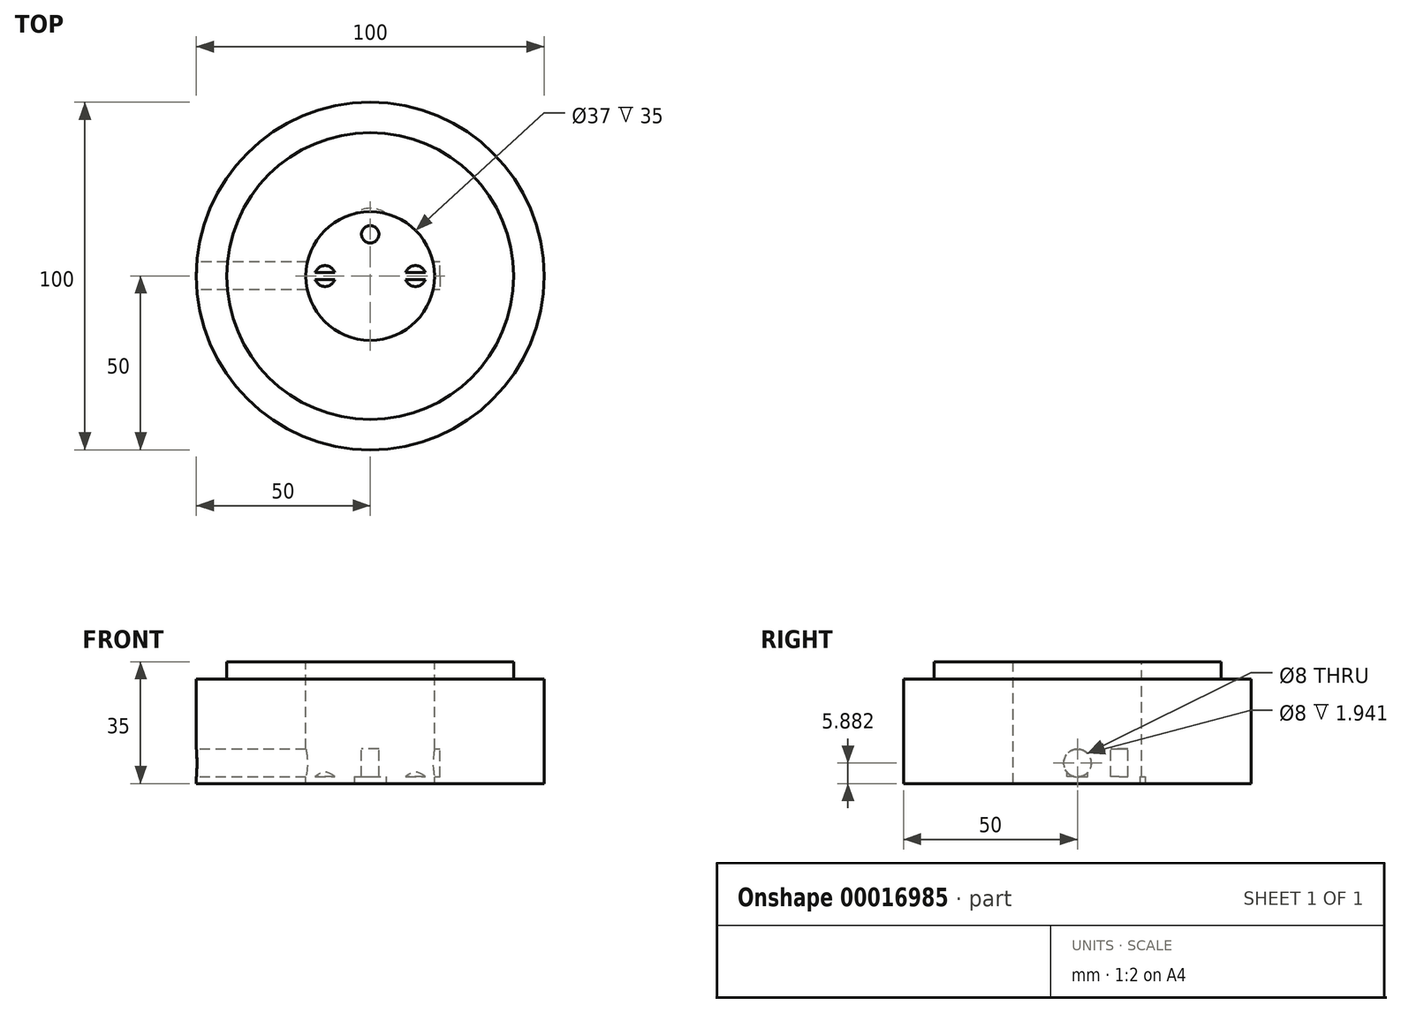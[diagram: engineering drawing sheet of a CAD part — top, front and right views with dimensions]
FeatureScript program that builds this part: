
annotation { "Feature Type Name" : "Feature", "Feature Type Description" : "" }
export const myFeature = defineFeature(function(context is Context, id is Id, definition is map)
    precondition{}
    {
        {
            var Q0;
            Q0=qCreatedBy(makeId("Top.planeOp"),FACE);
            var sketch = newSketch(context, id + "F0", { "sketchPlane" : qUnion([Q0])});
            skCircle(sketch, "E0", {"center": v(0, 0) * mm, "radius": 50 * mm});
            skSolve(sketch);
        }
        {
            var Q0;
            Q0=makeQuery(id+"F0.imprint","IMPRINT",FACE,{"disambiguationData":[TD([[makeQuery(id+"F0.imprint","IMPRINT",EDGE,{"derivedFrom":sQuery(id+"F0.wireOp",EDGE,"E0")}),1.0]])]});
            extrude(context, id + "F1", {"entities" : qUnion([Q0]), "depth" : 35 * mm});
        }
        {
            var Q0;
            Q0=makeQuery(id+"F1.opExtrude","CAP_FACE",FACE,{"disambiguationData":[OSD([sQuery(id+"F0.wireOp",EDGE,"E0")])],"isStart":false});
            var sketch = newSketch(context, id + "F2", { "sketchPlane" : qUnion([Q0])});
            skCircle(sketch, "E1", {"center": v(0, 0) * mm, "radius": 18.5 * mm});
            skSolve(sketch);
        }
        {
            var Q0;
            Q0=makeQuery(id+"F2.imprint","IMPRINT",FACE,{"disambiguationData":[TD([[makeQuery(id+"F2.imprint","IMPRINT",EDGE,{"derivedFrom":sQuery(id+"F2.wireOp",EDGE,"E1")}),1.0]])]});
            extrude(context, id + "F3", {"entities" : qUnion([Q0]), "operationType" : NewBodyOperationType.REMOVE, "oppositeDirection" : true, "depth" : 25 * mm});
        }
        {
            var Q0;
            Q0=makeQuery(id+"F1.opExtrude","CAP_FACE",FACE,{"disambiguationData":[OSD([sQuery(id+"F0.wireOp",EDGE,"E0")])],"isStart":false});
            var sketch = newSketch(context, id + "F4", { "sketchPlane" : qUnion([Q0])});
            skCircle(sketch, "E2", {"center": v(0, 0) * mm, "radius": 41.25 * mm});
            skCircle(sketch, "E3", {"center": v(0, 0) * mm, "radius": 50 * mm});
            skSolve(sketch);
        }
        {
            var Q0;
            Q0=makeQuery(id+"F4.imprint","IMPRINT",FACE,{"disambiguationData":[TD([[makeQuery(id+"F4.imprint","IMPRINT",EDGE,{"derivedFrom":sQuery(id+"F4.wireOp",EDGE,"E2")}),-1.0]])]});
            extrude(context, id + "F5", {"entities" : qUnion([Q0]), "operationType" : NewBodyOperationType.REMOVE, "oppositeDirection" : true, "depth" : 5 * mm});
        }
        {
            var Q0;
            Q0=qCreatedBy(makeId("Right.planeOp"),FACE);
            cPlane(context, id + "F6", {"entities" : qUnion([Q0]), "cplaneType" : CPlaneType.OFFSET, "offset" : 50 * mm, "oppositeDirection" : true, "width" : 150 * mm, "height" : 150 * mm});
        }
        {
            var Q0;
            Q0=qCreatedBy(id+"F6.planeOp",FACE);
            var sketch = newSketch(context, id + "F7", { "sketchPlane" : qUnion([Q0])});
            skCircle(sketch, "E4", {"center": v(0, 5.88) * mm, "radius": 4 * mm});
            skSolve(sketch);
        }
        {
            var Q0;
            Q0=makeQuery(id+"F7.imprint","IMPRINT",FACE,{"disambiguationData":[TD([[makeQuery(id+"F7.imprint","IMPRINT",EDGE,{"derivedFrom":sQuery(id+"F7.wireOp",EDGE,"E4")}),1.0]])]});
            extrude(context, id + "F8", {"entities" : qUnion([Q0]), "operationType" : NewBodyOperationType.REMOVE, "depth" : 70 * mm});
        }
        {
            var Q0;
            Q0=makeQuery(id+"F3.boolean.opBoolean","COPY",FACE,{"derivedFrom":makeQuery(id+"F3.opExtrude","CAP_FACE",FACE,{"disambiguationData":[OSD([sQuery(id+"F2.wireOp",EDGE,"E1")])],"isStart":false})});
            var sketch = newSketch(context, id + "F9", { "sketchPlane" : qUnion([Q0])});
            skCircle(sketch, "E5", {"center": v(-13, 0) * mm, "radius": 3 * mm});
            skCircle(sketch, "E6", {"center": v(13, 0) * mm, "radius": 3 * mm});
            skSolve(sketch);
        }
        {
            var Q0;
            Q0=makeQuery(id+"F9.imprint","IMPRINT",FACE,{"disambiguationData":[TD([[makeQuery(id+"F9.imprint","IMPRINT",EDGE,{"derivedFrom":sQuery(id+"F9.wireOp",EDGE,"E5")}),1.0]])]});
            var Q1;
            Q1=makeQuery(id+"F9.imprint","IMPRINT",FACE,{"disambiguationData":[TD([[makeQuery(id+"F9.imprint","IMPRINT",EDGE,{"derivedFrom":sQuery(id+"F9.wireOp",EDGE,"E6")}),1.0]])]});
            extrude(context, id + "F10", {"entities" : qUnion([Q0, Q1]), "operationType" : NewBodyOperationType.REMOVE, "oppositeDirection" : true, "depth" : 3 * mm});
        }
        {
            var Q0;
            Q0=makeQuery(id+"F3.boolean.opBoolean","COPY",FACE,{"derivedFrom":makeQuery(id+"F3.opExtrude","CAP_FACE",FACE,{"disambiguationData":[OSD([sQuery(id+"F2.wireOp",EDGE,"E1")])],"isStart":false})});
            var sketch = newSketch(context, id + "F11", { "sketchPlane" : qUnion([Q0])});
            skCircle(sketch, "E7", {"center": v(0, -12) * mm, "radius": 2.5 * mm});
            skLineSegment(sketch, "E8", {"start": v(-7.54, 0) * mm, "end": v(7.44, 0) * mm, "construction": true});
            skCircle(sketch, "E9.MirrorC", {"center": v(0, 12) * mm, "radius": 2.5 * mm});
            skSolve(sketch);
        }
        {
            var Q0;
            Q0=makeQuery(id+"F11.imprint","IMPRINT",FACE,{"disambiguationData":[TD([[makeQuery(id+"F11.imprint","IMPRINT",EDGE,{"derivedFrom":sQuery(id+"F11.wireOp",EDGE,"E7")}),1.0]])]});
            var Q1;
            Q1=makeQuery(id+"F11.imprint","IMPRINT",FACE,{"disambiguationData":[TD([[makeQuery(id+"F11.imprint","IMPRINT",EDGE,{"derivedFrom":sQuery(id+"F11.wireOp",EDGE,"E9.MirrorC")}),-1.0]])]});
            extrude(context, id + "F12", {"entities" : qUnion([Q0, Q1]), "operationType" : NewBodyOperationType.REMOVE, "oppositeDirection" : true, "depth" : 25 * mm});
        }
        {
            var Q0;
            Q0=makeQuery(id+"F1.opExtrude","CAP_FACE",FACE,{"disambiguationData":[OSD([sQuery(id+"F0.wireOp",EDGE,"E0")])],"isStart":true});
            var sketch = newSketch(context, id + "F13", { "sketchPlane" : qUnion([Q0])});
            skCircle(sketch, "E10", {"center": v(0, -12) * mm, "radius": 7.5 * mm});
            skLineSegment(sketch, "E11", {"start": v(11.17, 0) * mm, "end": v(-15.1, 0) * mm, "construction": true});
            skCircle(sketch, "E12.MirrorC", {"center": v(0, 12) * mm, "radius": 7.5 * mm});
            skSolve(sketch);
        }
        {
            var Q0;
            Q0=makeQuery(id+"F13.imprint","IMPRINT",FACE,{"disambiguationData":[TD([[makeQuery(id+"F13.imprint","IMPRINT",EDGE,{"derivedFrom":sQuery(id+"F13.wireOp",EDGE,"E12.MirrorC")}),-1.0]])]});
            var Q1;
            Q1=makeQuery(id+"F13.imprint","IMPRINT",FACE,{"disambiguationData":[TD([[makeQuery(id+"F13.imprint","IMPRINT",EDGE,{"derivedFrom":sQuery(id+"F13.wireOp",EDGE,"E10")}),1.0]])]});
            extrude(context, id + "F14", {"entities" : qUnion([Q0, Q1]), "operationType" : NewBodyOperationType.REMOVE, "oppositeDirection" : true, "depth" : 2 * mm});
        }
    });
